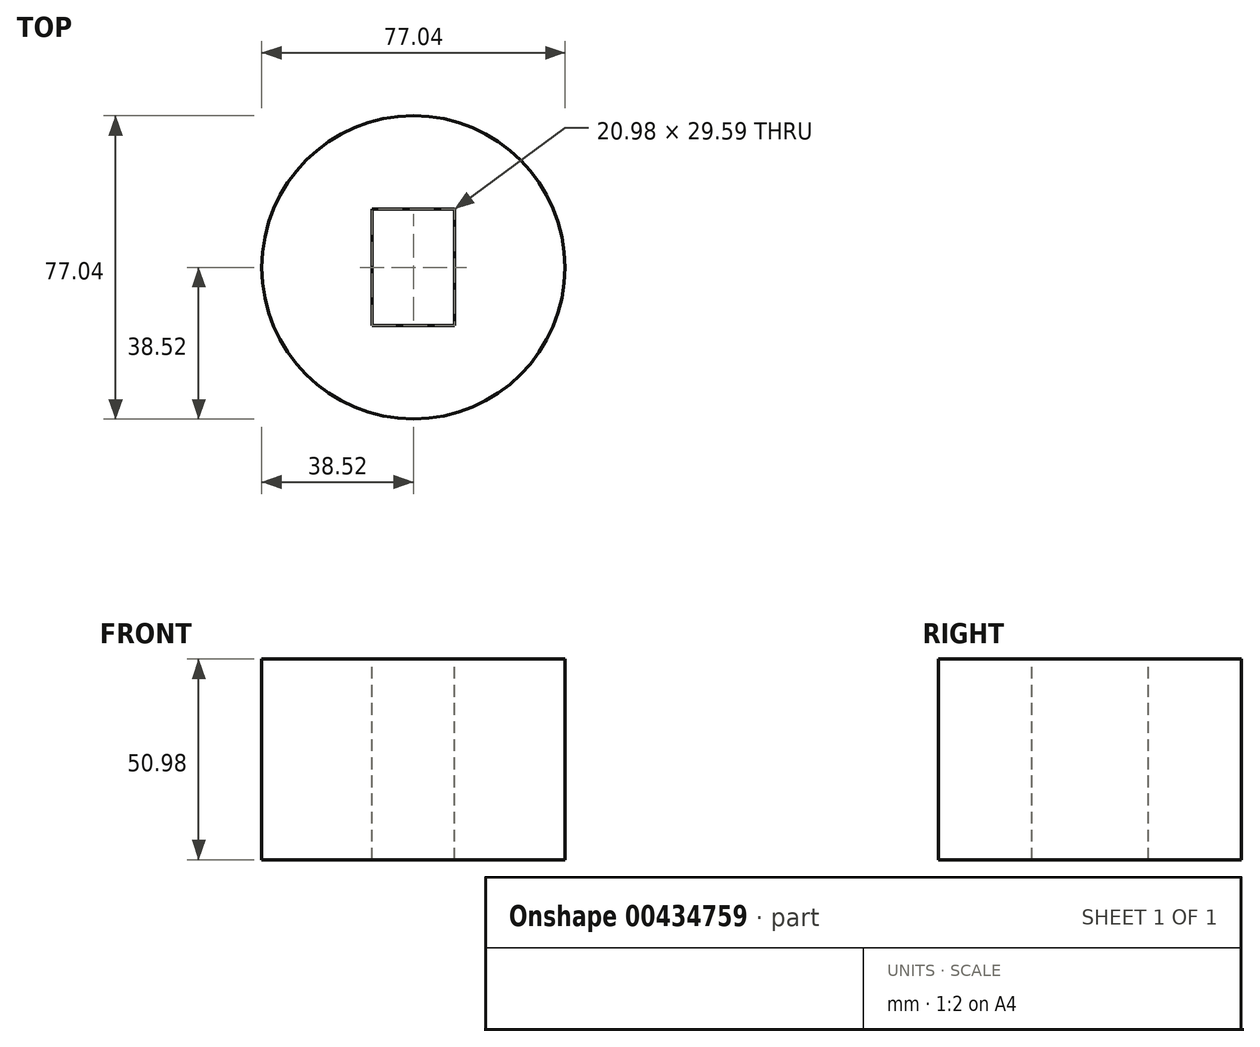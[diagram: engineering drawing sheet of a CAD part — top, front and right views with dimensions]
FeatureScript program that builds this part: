
annotation { "Feature Type Name" : "Feature", "Feature Type Description" : "" }
export const myFeature = defineFeature(function(context is Context, id is Id, definition is map)
    precondition{}
    {
        {
            var Q0;
            Q0=qCreatedBy(makeId("Right.planeOp"),FACE);
            var sketch = newSketch(context, id + "F0", { "sketchPlane" : qUnion([Q0])});
            skLineSegment(sketch, "E0", {"start": v(0, 0) * mm, "end": v(0, 50.98) * mm});
            skLineSegment(sketch, "E1", {"start": v(0, 50.98) * mm, "end": v(-38.52, 50.98) * mm});
            skLineSegment(sketch, "E2", {"start": v(-38.52, 50.98) * mm, "end": v(-38.52, 0) * mm});
            skLineSegment(sketch, "E3", {"start": v(-38.52, 0) * mm, "end": v(0, 0) * mm});
            skSolve(sketch);
        }
        {
            var Q0;
            Q0=makeQuery(id+"F0.imprint","IMPRINT",FACE,{"disambiguationData":[TD([[makeQuery(id+"F0.imprint","IMPRINT",EDGE,{"derivedFrom":sQuery(id+"F0.wireOp",EDGE,"E0")}),1.0]])]});
            var Q1;
            Q1=sQuery(id+"F0.wireOp",EDGE,"E0");
            revolve(context, id + "F1", {"entities" : qUnion([Q0]), "axis" : qUnion([Q1]), "revolveType" : RevolveType.FULL});
        }
        {
            var Q0;
            Q0=makeQuery(id+"F1.opRevolve","SWEPT_FACE",FACE,{"disambiguationData":[OSD([sQuery(id+"F0.wireOp",EDGE,"E1")])]});
            var sketch = newSketch(context, id + "F2", { "sketchPlane" : qUnion([Q0])});
            skLineSegment(sketch, "E4.bottom", {"start": v(10.49, -14.8) * mm, "end": v(-10.49, -14.8) * mm});
            skLineSegment(sketch, "E4.top", {"start": v(10.49, 14.8) * mm, "end": v(-10.49, 14.8) * mm});
            skLineSegment(sketch, "E4.left", {"start": v(10.49, -14.8) * mm, "end": v(10.49, 14.8) * mm});
            skLineSegment(sketch, "E4.right", {"start": v(-10.49, -14.8) * mm, "end": v(-10.49, 14.8) * mm});
            skPoint(sketch, "E4.middle", {"position": v(0, 0) * mm});
            skSolve(sketch);
        }
        {
            var Q0;
            Q0=makeQuery(id+"F2.imprint","IMPRINT",FACE,{"disambiguationData":[TD([[makeQuery(id+"F2.imprint","IMPRINT",EDGE,{"derivedFrom":sQuery(id+"F2.wireOp",EDGE,"E4.bottom")}),-1.0]])]});
            extrude(context, id + "F3", {"entities" : qUnion([Q0]), "operationType" : NewBodyOperationType.REMOVE, "endBound" : BoundingType.THROUGH_ALL, "oppositeDirection" : true, "depth" : 25.4 * mm});
        }
    });
